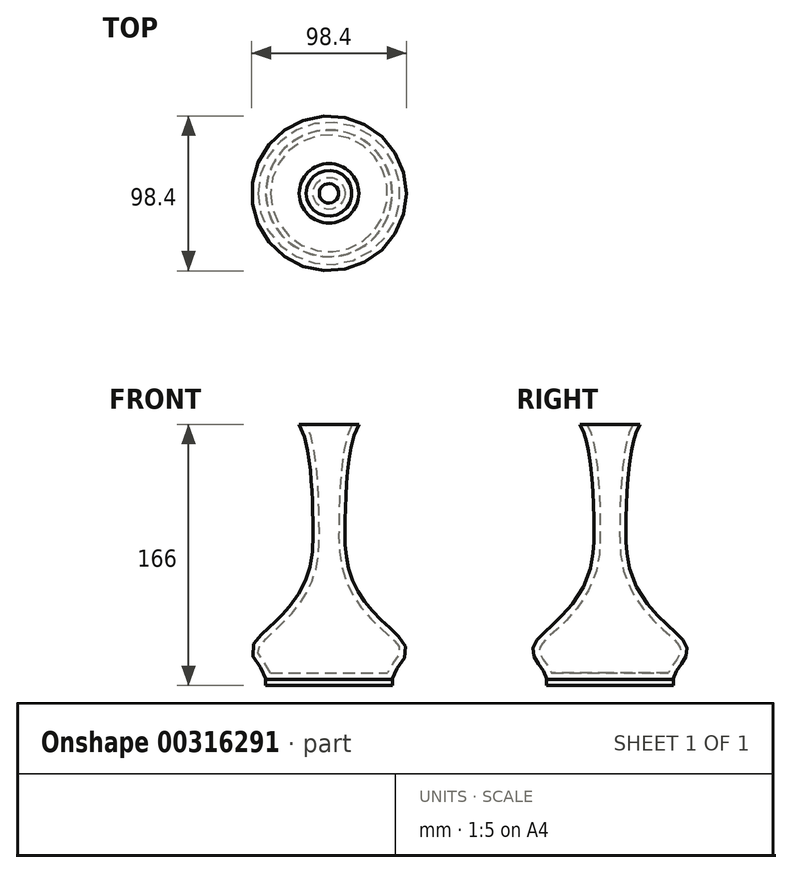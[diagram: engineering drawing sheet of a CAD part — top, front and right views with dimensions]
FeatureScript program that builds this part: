
annotation { "Feature Type Name" : "Feature", "Feature Type Description" : "" }
export const myFeature = defineFeature(function(context is Context, id is Id, definition is map)
    precondition{}
    {
        {
            var Q0;
            Q0=qCreatedBy(makeId("Top.planeOp"),FACE);
            var sketch = newSketch(context, id + "F0", { "sketchPlane" : qUnion([Q0])});
            skCircle(sketch, "E0", {"center": v(0, 0) * mm, "radius": 40 * mm});
            skSolve(sketch);
        }
        {
            var Q0;
            Q0=makeQuery(id+"F0.imprint","IMPRINT",FACE,{"disambiguationData":[TD([[makeQuery(id+"F0.imprint","IMPRINT",EDGE,{"derivedFrom":sQuery(id+"F0.wireOp",EDGE,"E0")}),1.0]])]});
            cPlane(context, id + "F1", {"entities" : qUnion([Q0]), "cplaneType" : CPlaneType.OFFSET, "offset" : 4 * mm, "width" : 150 * mm, "height" : 150 * mm});
        }
        {
            var Q0;
            Q0=qCreatedBy(id+"F1.planeOp",FACE);
            var sketch = newSketch(context, id + "F2", { "sketchPlane" : qUnion([Q0])});
            skCircle(sketch, "E1", {"center": v(0, 0) * mm, "radius": 41.51 * mm});
            skSolve(sketch);
        }
        {
            var Q0;
            Q0=makeQuery(id+"F2.imprint","IMPRINT",FACE,{"disambiguationData":[TD([[makeQuery(id+"F2.imprint","IMPRINT",EDGE,{"derivedFrom":sQuery(id+"F2.wireOp",EDGE,"E1")}),1.0]])]});
            cPlane(context, id + "F3", {"entities" : qUnion([Q0]), "cplaneType" : CPlaneType.OFFSET, "offset" : 6 * mm, "width" : 150 * mm, "height" : 150 * mm});
        }
        {
            var Q0;
            Q0=qCreatedBy(id+"F3.planeOp",FACE);
            var sketch = newSketch(context, id + "F4", { "sketchPlane" : qUnion([Q0])});
            skCircle(sketch, "E2", {"center": v(0, 0) * mm, "radius": 45.5 * mm});
            skSolve(sketch);
        }
        {
            var Q0;
            Q0=makeQuery(id+"F4.imprint","IMPRINT",FACE,{"disambiguationData":[TD([[makeQuery(id+"F4.imprint","IMPRINT",EDGE,{"derivedFrom":sQuery(id+"F4.wireOp",EDGE,"E2")}),1.0]])]});
            cPlane(context, id + "F5", {"entities" : qUnion([Q0]), "cplaneType" : CPlaneType.OFFSET, "offset" : 8 * mm, "width" : 150 * mm, "height" : 150 * mm});
        }
        {
            var Q0;
            Q0=qCreatedBy(id+"F5.planeOp",FACE);
            var sketch = newSketch(context, id + "F6", { "sketchPlane" : qUnion([Q0])});
            skCircle(sketch, "E3", {"center": v(0, 0) * mm, "radius": 49.2 * mm});
            skSolve(sketch);
        }
        {
            var Q0;
            Q0=makeQuery(id+"F6.imprint","IMPRINT",FACE,{"disambiguationData":[TD([[makeQuery(id+"F6.imprint","IMPRINT",EDGE,{"derivedFrom":sQuery(id+"F6.wireOp",EDGE,"E3")}),1.0]])]});
            cPlane(context, id + "F7", {"entities" : qUnion([Q0]), "cplaneType" : CPlaneType.OFFSET, "offset" : 6 * mm, "width" : 150 * mm, "height" : 150 * mm});
        }
        {
            var Q0;
            Q0=qCreatedBy(id+"F7.planeOp",FACE);
            var sketch = newSketch(context, id + "F8", { "sketchPlane" : qUnion([Q0])});
            skCircle(sketch, "E4", {"center": v(0, 0) * mm, "radius": 47 * mm});
            skSolve(sketch);
        }
        {
            var Q0;
            Q0=qCreatedBy(id+"F7.planeOp",FACE);
            cPlane(context, id + "F9", {"entities" : qUnion([Q0]), "cplaneType" : CPlaneType.OFFSET, "offset" : 6 * mm, "width" : 150 * mm, "height" : 150 * mm});
        }
        {
            var Q0;
            Q0=qCreatedBy(id+"F9.planeOp",FACE);
            var sketch = newSketch(context, id + "F10", { "sketchPlane" : qUnion([Q0])});
            skCircle(sketch, "E5", {"center": v(0, 0) * mm, "radius": 41.44 * mm});
            skSolve(sketch);
        }
        {
            var Q0;
            Q0=qCreatedBy(id+"F9.planeOp",FACE);
            cPlane(context, id + "F11", {"entities" : qUnion([Q0]), "cplaneType" : CPlaneType.OFFSET, "offset" : 16 * mm, "width" : 150 * mm, "height" : 150 * mm});
        }
        {
            var Q0;
            Q0=qCreatedBy(id+"F11.planeOp",FACE);
            var sketch = newSketch(context, id + "F12", { "sketchPlane" : qUnion([Q0])});
            skCircle(sketch, "E6", {"center": v(0, 0) * mm, "radius": 25.29 * mm});
            skSolve(sketch);
        }
        {
            var Q0;
            Q0=qCreatedBy(id+"F11.planeOp",FACE);
            cPlane(context, id + "F13", {"entities" : qUnion([Q0]), "cplaneType" : CPlaneType.OFFSET, "offset" : 25 * mm, "width" : 150 * mm, "height" : 150 * mm});
        }
        {
            var Q0;
            Q0=qCreatedBy(id+"F13.planeOp",FACE);
            var sketch = newSketch(context, id + "F14", { "sketchPlane" : qUnion([Q0])});
            skCircle(sketch, "E7", {"center": v(0, 0) * mm, "radius": 12.22 * mm});
            skSolve(sketch);
        }
        {
            var Q0;
            Q0=qCreatedBy(id+"F13.planeOp",FACE);
            cPlane(context, id + "F15", {"entities" : qUnion([Q0]), "cplaneType" : CPlaneType.OFFSET, "offset" : 25 * mm, "width" : 150 * mm, "height" : 150 * mm});
        }
        {
            var Q0;
            Q0=qCreatedBy(id+"F15.planeOp",FACE);
            var sketch = newSketch(context, id + "F16", { "sketchPlane" : qUnion([Q0])});
            skCircle(sketch, "E8", {"center": v(0, 0) * mm, "radius": 10.18 * mm});
            skSolve(sketch);
        }
        {
            var Q0;
            Q0=qCreatedBy(id+"F15.planeOp",FACE);
            cPlane(context, id + "F17", {"entities" : qUnion([Q0]), "cplaneType" : CPlaneType.OFFSET, "offset" : 25 * mm, "width" : 150 * mm, "height" : 150 * mm});
        }
        {
            var Q0;
            Q0=qCreatedBy(id+"F17.planeOp",FACE);
            var sketch = newSketch(context, id + "F18", { "sketchPlane" : qUnion([Q0])});
            skCircle(sketch, "E9", {"center": v(0, 0) * mm, "radius": 11 * mm});
            skSolve(sketch);
        }
        {
            var Q0;
            Q0=qCreatedBy(id+"F17.planeOp",FACE);
            cPlane(context, id + "F19", {"entities" : qUnion([Q0]), "cplaneType" : CPlaneType.OFFSET, "offset" : 25 * mm, "width" : 150 * mm, "height" : 150 * mm});
        }
        {
            var Q0;
            Q0=qCreatedBy(id+"F19.planeOp",FACE);
            var sketch = newSketch(context, id + "F20", { "sketchPlane" : qUnion([Q0])});
            skCircle(sketch, "E10", {"center": v(0, 0) * mm, "radius": 13.75 * mm});
            skSolve(sketch);
        }
        {
            var Q0;
            Q0=qCreatedBy(id+"F19.planeOp",FACE);
            cPlane(context, id + "F21", {"entities" : qUnion([Q0]), "cplaneType" : CPlaneType.OFFSET, "offset" : 10 * mm, "width" : 150 * mm, "height" : 150 * mm});
        }
        {
            var Q0;
            Q0=qCreatedBy(id+"F21.planeOp",FACE);
            var sketch = newSketch(context, id + "F22", { "sketchPlane" : qUnion([Q0])});
            skCircle(sketch, "E11", {"center": v(0, 0) * mm, "radius": 16.33 * mm});
            skSolve(sketch);
        }
        {
            var Q0;
            Q0=qCreatedBy(id+"F21.planeOp",FACE);
            cPlane(context, id + "F23", {"entities" : qUnion([Q0]), "cplaneType" : CPlaneType.OFFSET, "offset" : 6 * mm, "width" : 150 * mm, "height" : 150 * mm});
        }
        {
            var Q0;
            Q0=qCreatedBy(id+"F23.planeOp",FACE);
            var sketch = newSketch(context, id + "F24", { "sketchPlane" : qUnion([Q0])});
            skCircle(sketch, "E12", {"center": v(0, 0) * mm, "radius": 18.94 * mm});
            skSolve(sketch);
        }
        {
            var Q0;
            Q0=qSketchRegion(id+"F0",true);
            var Q1;
            Q1=qSketchRegion(id+"F2",true);
            var Q2;
            Q2=qSketchRegion(id+"F4",true);
            var Q3;
            Q3=qSketchRegion(id+"F6",true);
            var Q4;
            Q4=qSketchRegion(id+"F8",true);
            var Q5;
            Q5=qSketchRegion(id+"F10",true);
            var Q6;
            Q6=qSketchRegion(id+"F12",true);
            var Q7;
            Q7=qSketchRegion(id+"F14",true);
            var Q8;
            Q8=qSketchRegion(id+"F16",true);
            var Q9;
            Q9=qSketchRegion(id+"F18",true);
            var Q10;
            Q10=qSketchRegion(id+"F20",true);
            var Q11;
            Q11=qSketchRegion(id+"F22",true);
            var Q12;
            Q12=qSketchRegion(id+"F24",true);
            loft(context, id + "F25", {"sheetProfilesArray" : [{ "sheetProfileEntities" : qUnion([Q0]) }, { "sheetProfileEntities" : qUnion([Q1]) }, { "sheetProfileEntities" : qUnion([Q2]) }, { "sheetProfileEntities" : qUnion([Q3]) }, { "sheetProfileEntities" : qUnion([Q4]) }, { "sheetProfileEntities" : qUnion([Q5]) }, { "sheetProfileEntities" : qUnion([Q6]) }, { "sheetProfileEntities" : qUnion([Q7]) }, { "sheetProfileEntities" : qUnion([Q8]) }, { "sheetProfileEntities" : qUnion([Q9]) }, { "sheetProfileEntities" : qUnion([Q10]) }, { "sheetProfileEntities" : qUnion([Q11]) }, { "sheetProfileEntities" : qUnion([Q12]) }]});
        }
        {
            var Q0;
            Q0=makeQuery(id+"F25.opLoft","CAP_FACE",FACE,{"disambiguationData":[OSD([makeQuery(id+"F24.imprint","IMPRINT",FACE,{"disambiguationData":[TD([[makeQuery(id+"F24.imprint","IMPRINT",EDGE,{"derivedFrom":sQuery(id+"F24.wireOp",EDGE,"E12")}),1.0]])]})])],"isStart":true});
            shell(context, id + "F26", {"entities" : qUnion([Q0]), "thickness" : 4 * mm});
        }
        {
            var Q0;
            Q0=qCreatedBy(makeId("Top.planeOp"),FACE);
            var sketch = newSketch(context, id + "F27", { "sketchPlane" : qUnion([Q0])});
            skCircle(sketch, "E13", {"center": v(0, 0) * mm, "radius": 40.24 * mm});
            skSolve(sketch);
        }
        {
            var Q0;
            Q0=qSketchRegion(id+"F27",true);
            extrude(context, id + "F28", {"entities" : qUnion([Q0]), "operationType" : NewBodyOperationType.ADD, "oppositeDirection" : true, "depth" : 4 * mm});
        }
    });
